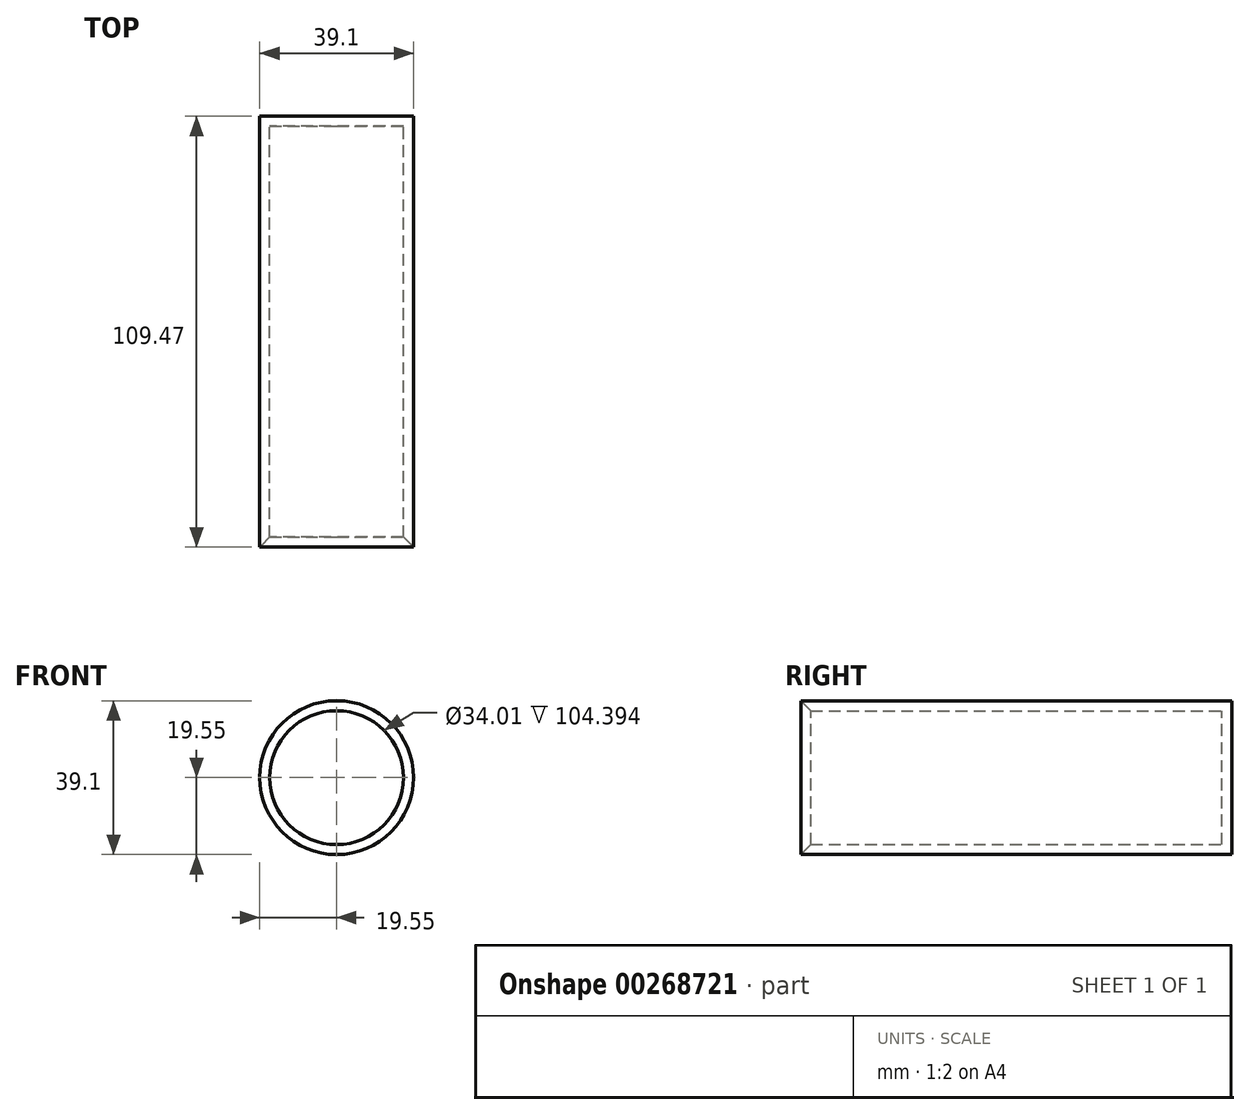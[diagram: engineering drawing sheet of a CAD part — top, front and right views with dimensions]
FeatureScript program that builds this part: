
annotation { "Feature Type Name" : "Feature", "Feature Type Description" : "" }
export const myFeature = defineFeature(function(context is Context, id is Id, definition is map)
    precondition{}
    {
        {
            var Q0;
            Q0=qCreatedBy(makeId("Front.planeOp"),FACE);
            var sketch = newSketch(context, id + "F0", { "sketchPlane" : qUnion([Q0])});
            skCircle(sketch, "E0", {"center": v(0, 0) * mm, "radius": 21.9 * mm});
            skCircle(sketch, "E1", {"center": v(0, 0) * mm, "radius": 19.55 * mm});
            skSolve(sketch);
        }
        {
            var Q0;
            Q0=makeQuery(id+"F0.imprint","IMPRINT",FACE,{"disambiguationData":[TD([[makeQuery(id+"F0.imprint","IMPRINT",EDGE,{"derivedFrom":sQuery(id+"F0.wireOp",EDGE,"E1")}),1.0]])]});
            extrude(context, id + "F1", {"entities" : qUnion([Q0]), "depth" : 112.01 * mm});
        }
        {
            var Q0;
            Q0=makeQuery(id+"F1.opExtrude","CAP_FACE",FACE,{"disambiguationData":[OSD([sQuery(id+"F0.wireOp",EDGE,"E1")])],"isStart":false});
            shell(context, id + "F2", {"entities" : qUnion([Q0]), "thickness" : 2.54 * mm});
        }
        {
            var Q0;
            {var subQ0=sQuery(id+"F0.wireOp",EDGE,"E1");Q0=makeQuery(id+"F2.opShell","OFFSET_EDGE",EDGE,{"disambiguationData":[OSD([subQ0]),TDD([makeQuery(id+"F1.opExtrude","CAP_EDGE",EDGE,{"disambiguationData":[OSD([subQ0])],"isStart":false})])]});}
            chamfer(context, id + "F3", {"entities" : qUnion([Q0]), "width" : 5.08 * mm, "tangentPropagation" : true});
        }
    });
